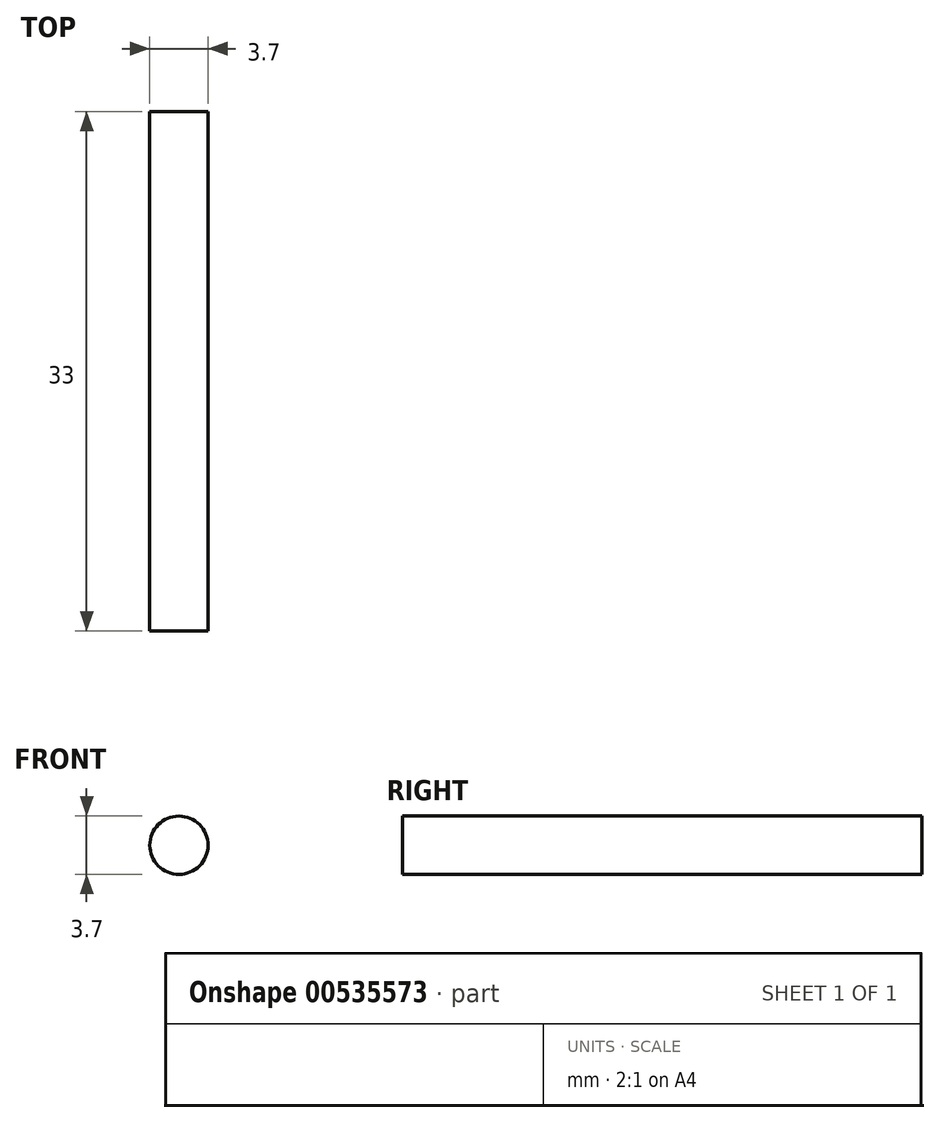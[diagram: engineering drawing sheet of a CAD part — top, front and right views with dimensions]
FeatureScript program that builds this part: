
annotation { "Feature Type Name" : "Feature", "Feature Type Description" : "" }
export const myFeature = defineFeature(function(context is Context, id is Id, definition is map)
    precondition{}
    {
        {
            var Q0;
            Q0=qCreatedBy(makeId("Front.planeOp"),FACE);
            var sketch = newSketch(context, id + "F0", { "sketchPlane" : qUnion([Q0])});
            skCircle(sketch, "E0", {"center": v(0, 0) * mm, "radius": 1.85 * mm});
            skSolve(sketch);
        }
        {
            var Q0;
            Q0 = qSketchRegion(id + "F0", true);
            extrude(context, id + "F1", {"entities" : qUnion([Q0]), "depth" : 33 * mm, "offsetDistance" : 25 * mm, "symmetric" : true});
        }
    });
